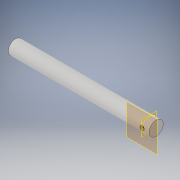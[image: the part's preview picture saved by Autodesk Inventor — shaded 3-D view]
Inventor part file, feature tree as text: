
AUTODESK INVENTOR PART (.ipt)
format: ipt  version: 2019 (Build 230136000, 136)  size: 104,960 bytes
history: native  units: in
note: dims shown in document units (in); Inventor stores cm internally (conversion verified against a paired STEP export)
features: sketch x3, extrude x2, plane x2, projected_geometry x1
ambient origin geometry x8: Origin, YZ Plane, XZ Plane, XY Plane, X Axis, Y Axis, Z Axis, Center Point
bodies: Solid1 (feature_tree)
feature tree (8):
  extrude  "Extrusion1"  Depth=0.3937in TaperAngle=0.0deg
  plane  "Work Plane1"
  sketch  "Sketch2"  dims[d3=-0.1969in d4=0.122in]
  plane  "Work Plane2"
  extrude  "Extrusion2"  Depth=0.122in
  sketch  "Sketch1"  dims[d0=0.3937in d1=3.937in d2=0.0in]
  projected_geometry  "Projected Loop1"
  sketch  "Sketch3"  dims[d5=0.1969in d6=0.0in]
